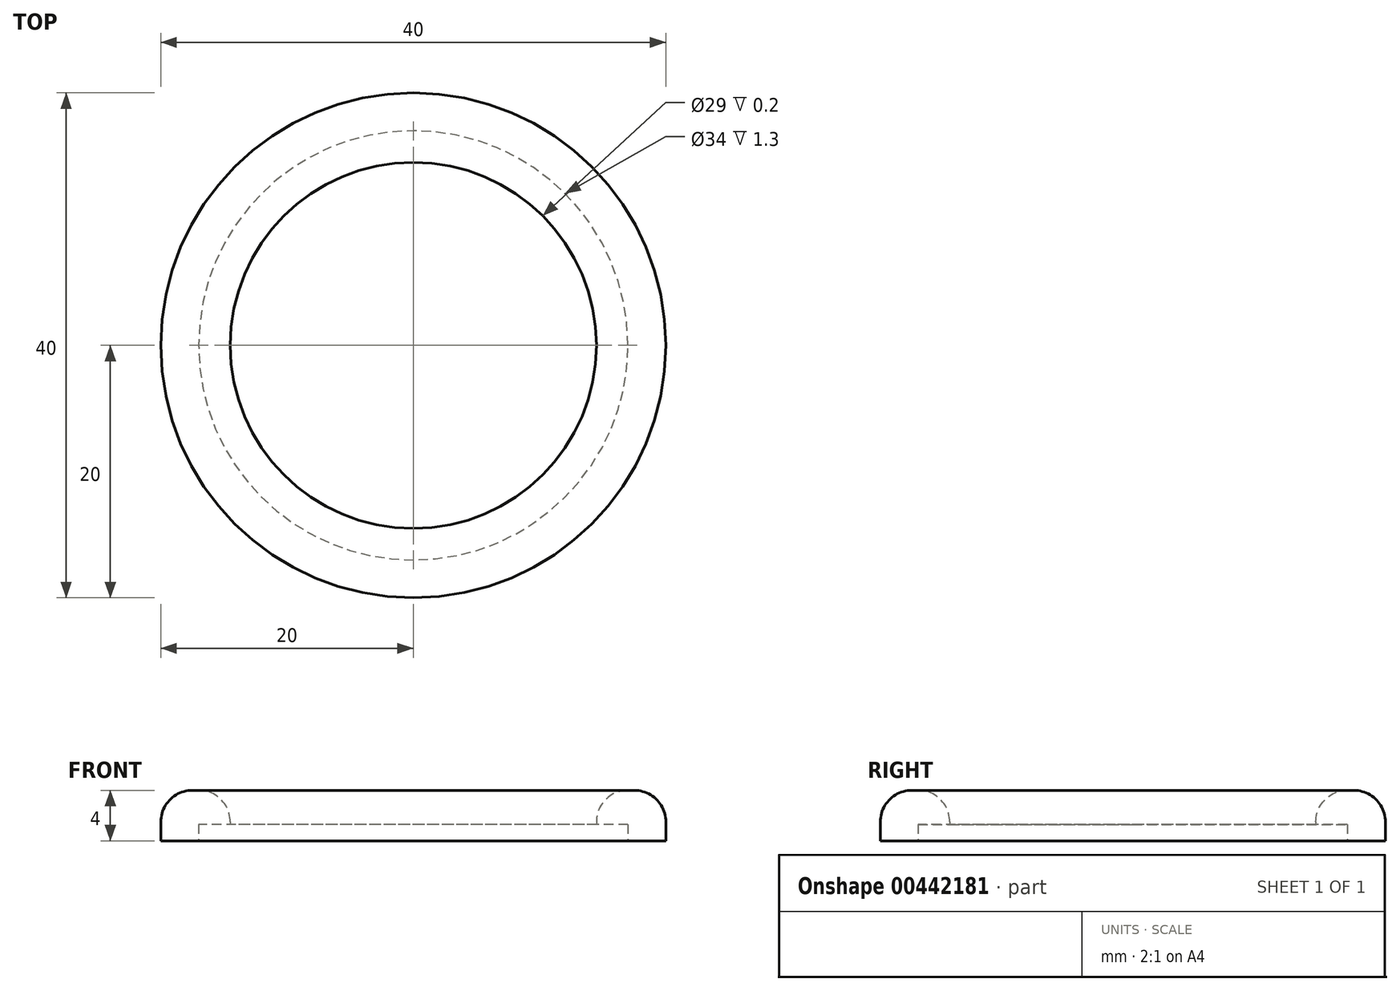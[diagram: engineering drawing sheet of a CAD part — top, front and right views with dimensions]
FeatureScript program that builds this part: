
annotation { "Feature Type Name" : "Feature", "Feature Type Description" : "" }
export const myFeature = defineFeature(function(context is Context, id is Id, definition is map)
    precondition{}
    {
        {
            var Q0;
            Q0=qCreatedBy(makeId("Top.planeOp"),FACE);
            var sketch = newSketch(context, id + "F0", { "sketchPlane" : qUnion([Q0])});
            skCircle(sketch, "E0", {"center": v(0, 0) * mm, "radius": 20 * mm});
            skCircle(sketch, "E1", {"center": v(0, 0) * mm, "radius": 14.5 * mm});
            skSolve(sketch);
        }
        {
            var Q0;
            Q0=makeQuery(id+"F0.imprint","IMPRINT",FACE,{"disambiguationData":[TD([[makeQuery(id+"F0.imprint","IMPRINT",EDGE,{"derivedFrom":sQuery(id+"F0.wireOp",EDGE,"E0")}),1.0]])]});
            extrude(context, id + "F1", {"entities" : qUnion([Q0]), "depth" : 4 * mm});
        }
        {
            var Q0;
            Q0=makeQuery(id+"F1.opExtrude","CAP_EDGE",EDGE,{"disambiguationData":[OSD([sQuery(id+"F0.wireOp",EDGE,"E1")])],"isStart":false});
            var Q1;
            Q1=makeQuery(id+"F1.opExtrude","CAP_EDGE",EDGE,{"disambiguationData":[OSD([sQuery(id+"F0.wireOp",EDGE,"E0")])],"isStart":false});
            fillet(context, id + "F2", {"entities" : qUnion([Q0, Q1]), "radius" : 2.5 * mm, "tangentPropagation" : true, "allowEdgeOverflow" : false});
        }
        {
            var Q0;
            Q0=qCreatedBy(makeId("Top.planeOp"),FACE);
            var sketch = newSketch(context, id + "F3", { "sketchPlane" : qUnion([Q0])});
            skCircle(sketch, "E2", {"center": v(0, 0) * mm, "radius": 17 * mm});
            skSolve(sketch);
        }
        {
            var Q0;
            Q0 = qSketchRegion(id + "F3", true);
            extrude(context, id + "F4", {"entities" : qUnion([Q0]), "operationType" : NewBodyOperationType.REMOVE, "depth" : 1.3 * mm});
        }
    });
